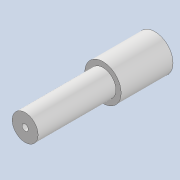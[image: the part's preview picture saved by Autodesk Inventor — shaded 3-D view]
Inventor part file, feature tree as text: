
AUTODESK INVENTOR PART (.ipt)
format: ipt  version: 2020 (Build 240168000, 168)  size: 131,584 bytes
history: native  units: mm
features: extrude x3, sketch x3, other x3, fillet x2, reference x1, projected_geometry x1
ambient origin geometry x8: Origin, YZ Plane, XZ Plane, XY Plane, X Axis, Y Axis, Z Axis, Center Point
bodies: Solid1 (feature_tree)
feature tree (13):
  extrude  "Extrusion1"  Depth=3.0mm
  extrude  "Extrusion2"  Depth=2.0mm TaperAngle=0.0deg
  extrude  "Extrusion3"  Depth=3.0mm
  fillet  "Fillet1"  Radius=15.0mm
  fillet  "Fillet2"  Radius=40.0mm
  sketch  "Sketch1"  dims[d0=3.0mm d1=7.0mm]
  reference  "Reference1"
  sketch  "Sketch2"  dims[d2=8.0mm d3=0.0mm d4=2.0mm d5=0.0mm]
  sketch  "Sketch3"  dims[d6=1.2mm d7=5.0mm d8=15.0mm d9=0.0mm d10=40.0mm d11=3.0mm]
  projected_geometry  "Projected Loop1"
  parser-record x1  (decoder bookkeeping rows leaked as tree rows — omitted from the tree; the rows remain in map.json)
  other  "tip_ass_t1.iam"
  other  "pin_3_30:1"
note: 1 file-system path scrubbed to <path> (originals preserved in map.json)
